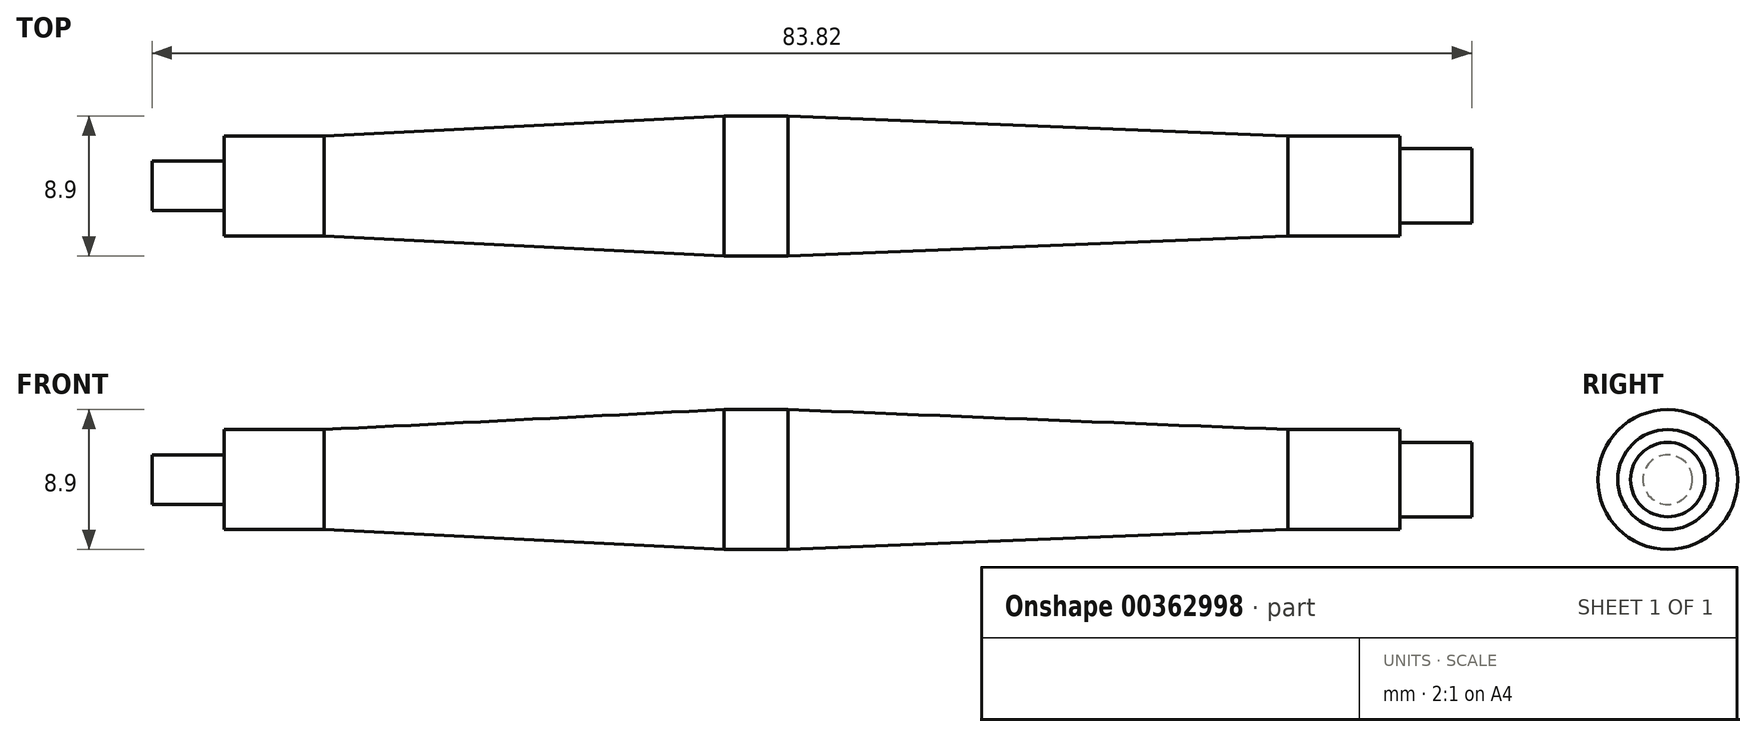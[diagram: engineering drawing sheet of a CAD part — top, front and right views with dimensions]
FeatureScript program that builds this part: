
annotation { "Feature Type Name" : "Feature", "Feature Type Description" : "" }
export const myFeature = defineFeature(function(context is Context, id is Id, definition is map)
    precondition{}
    {
        {
            var Q0;
            Q0=qCreatedBy(makeId("Front.planeOp"),FACE);
            var sketch = newSketch(context, id + "F0", { "sketchPlane" : qUnion([Q0])});
            skLineSegment(sketch, "E0", {"start": v(-42.5, 0) * mm, "end": v(41.32, 0) * mm});
            skLineSegment(sketch, "E1", {"start": v(36.75, 2.36) * mm, "end": v(36.75, 3.18) * mm});
            skLineSegment(sketch, "E2", {"start": v(-37.93, 1.57) * mm, "end": v(-37.93, 3.18) * mm});
            skLineSegment(sketch, "E3.0", {"start": v(-37.93, 3.18) * mm, "end": v(-31.58, 3.18) * mm});
            skLineSegment(sketch, "E4.0", {"start": v(-6.18, 4.45) * mm, "end": v(-2.11, 4.45) * mm});
            skLineSegment(sketch, "E5", {"start": v(-31.58, 3.18) * mm, "end": v(-6.18, 4.45) * mm});
            skLineSegment(sketch, "E6", {"start": v(-2.11, 4.45) * mm, "end": v(29.64, 3.18) * mm});
            skLineSegment(sketch, "E7.trimOffspring", {"start": v(29.64, 3.18) * mm, "end": v(36.75, 3.18) * mm});
            skLineSegment(sketch, "E8.0", {"start": v(41.32, 0) * mm, "end": v(41.32, 2.36) * mm});
            skLineSegment(sketch, "E9.0", {"start": v(-42.5, 0) * mm, "end": v(-42.5, 1.57) * mm});
            skLineSegment(sketch, "E10", {"start": v(36.75, 2.36) * mm, "end": v(41.32, 2.36) * mm});
            skLineSegment(sketch, "E11.0", {"start": v(-42.5, 1.57) * mm, "end": v(-37.93, 1.57) * mm});
            skPoint(sketch, "E12.orphan", {"position": v(-37.93, 0) * mm});
            skSolve(sketch);
        }
        {
            var Q0;
            Q0=makeQuery(id+"F0.imprint","IMPRINT",FACE,{"disambiguationData":[TD([[makeQuery(id+"F0.imprint","IMPRINT",EDGE,{"derivedFrom":sQuery(id+"F0.wireOp",EDGE,"E0")}),1.0]])]});
            var Q1;
            Q1=sQuery(id+"F0.wireOp",EDGE,"E0");
            revolve(context, id + "F1", {"entities" : qUnion([Q0]), "axis" : qUnion([Q1]), "revolveType" : RevolveType.FULL});
        }
    });
